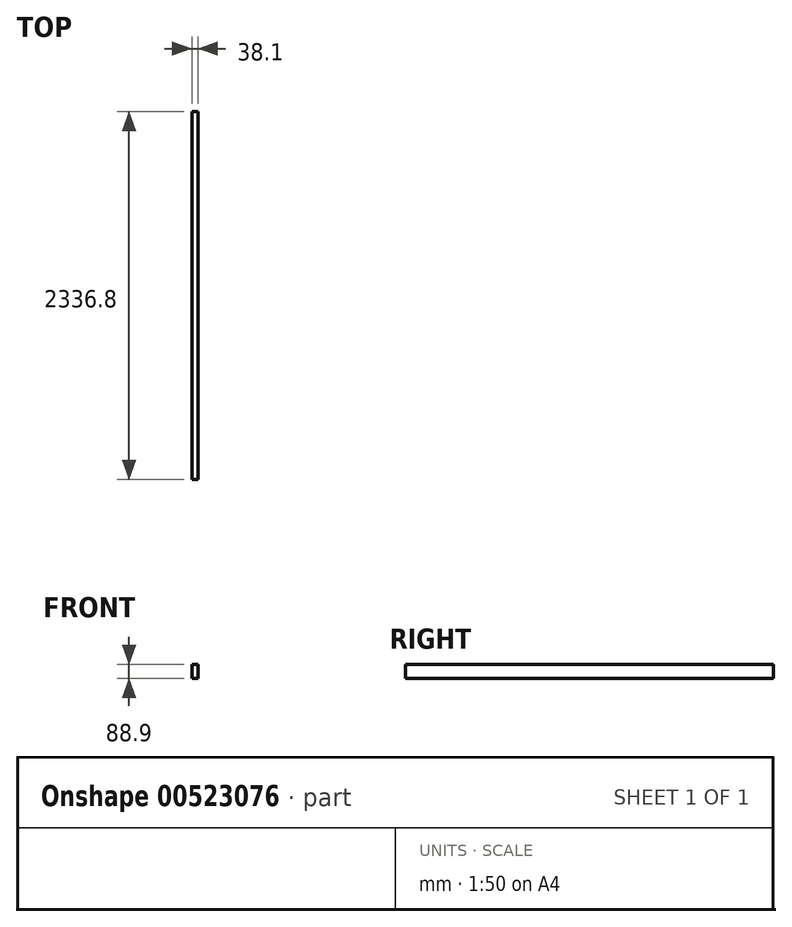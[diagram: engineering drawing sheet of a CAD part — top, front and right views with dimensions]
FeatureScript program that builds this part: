
annotation { "Feature Type Name" : "Feature", "Feature Type Description" : "" }
export const myFeature = defineFeature(function(context is Context, id is Id, definition is map)
    precondition{}
    {
        {
            var Q0;
            Q0=qCreatedBy(makeId("Front.planeOp"),FACE);
            var sketch = newSketch(context, id + "F0", { "sketchPlane" : qUnion([Q0])});
            skLineSegment(sketch, "E0.bottom", {"start": v(0, 0) * mm, "end": v(38.1, 0) * mm});
            skLineSegment(sketch, "E0.top", {"start": v(0, 88.9) * mm, "end": v(38.1, 88.9) * mm});
            skLineSegment(sketch, "E0.left", {"start": v(0, 0) * mm, "end": v(0, 88.9) * mm});
            skLineSegment(sketch, "E0.right", {"start": v(38.1, 0) * mm, "end": v(38.1, 88.9) * mm});
            skSolve(sketch);
        }
        {
            var Q0;
            Q0=qSketchRegion(id+"F0",true);
            extrude(context, id + "F1", {"entities" : qUnion([Q0]), "depth" : 2336.8 * mm, "offsetDistance" : 25.4 * mm});
        }
    });
